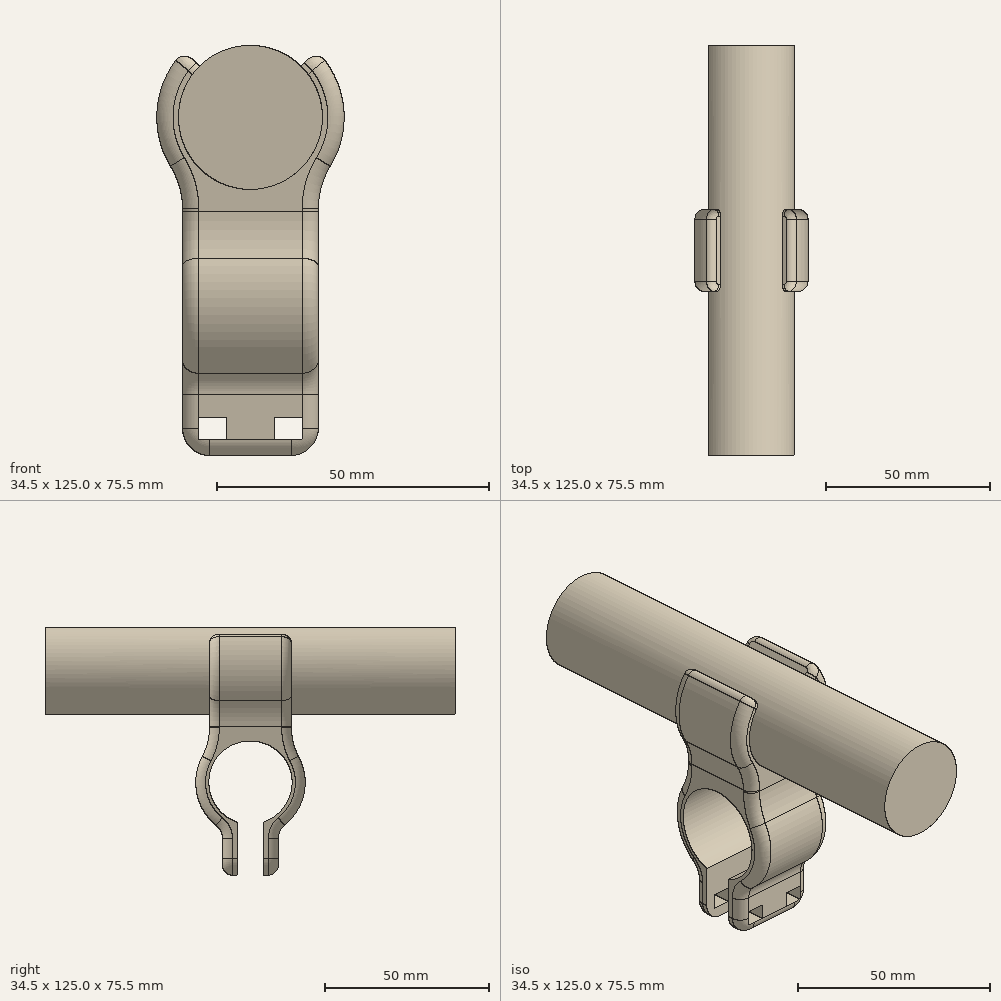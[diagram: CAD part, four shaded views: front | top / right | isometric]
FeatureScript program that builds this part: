
annotation { "Feature Type Name" : "Feature", "Feature Type Description" : "" }
export const myFeature = defineFeature(function(context is Context, id is Id, definition is map)
    precondition{}
    {
        {
            var Q0;
            Q0=qCreatedBy(makeId("Front.planeOp"),FACE);
            var sketch = newSketch(context, id + "F0", { "sketchPlane" : qUnion([Q0])});
            skCircle(sketch, "E0", {"center": v(0, 0) * mm, "radius": 13.25 * mm});
            skSolve(sketch);
        }
        {
            var Q0;
            Q0 = qSketchRegion(id + "F0", true);
            extrude(context, id + "F1", {"entities" : qUnion([Q0]), "endBound" : BoundingType.SYMMETRIC, "depth" : 125 * mm, "offsetDistance" : 25 * mm});
        }
        {
            var Q0;
            Q0=qCreatedBy(makeId("Front.planeOp"),FACE);
            var sketch = newSketch(context, id + "F2", { "sketchPlane" : qUnion([Q0])});
            skArc(sketch, "E1", {"start": v(-12.2, 12.2) * mm, "mid": v(0, -17.25) * mm, "end": v(12.2, 12.2) * mm});
            skArc(sketch, "E2", {"start": v(-9.37, 9.37) * mm, "mid": v(0, -13.25) * mm, "end": v(9.37, 9.37) * mm});
            skLineSegment(sketch, "E3", {"start": v(-9.37, 9.37) * mm, "end": v(-12.2, 12.2) * mm});
            skLineSegment(sketch, "E4", {"start": v(9.37, 9.37) * mm, "end": v(12.2, 12.2) * mm});
            skLineSegment(sketch, "E5", {"start": v(12.2, 12.2) * mm, "end": v(-12.2, 12.2) * mm, "construction": true});
            skSolve(sketch);
        }
        {
            var Q0;
            Q0 = qSketchRegion(id + "F2", true);
            extrude(context, id + "F3", {"entities" : qUnion([Q0]), "endBound" : BoundingType.SYMMETRIC, "depth" : 25 * mm, "offsetDistance" : 25 * mm});
        }
        {
            var Q0;
            Q0=qCreatedBy(makeId("Right.planeOp"),FACE);
            var sketch = newSketch(context, id + "F4", { "sketchPlane" : qUnion([Q0])});
            skArc(sketch, "E6", {"start": v(4, -46.05) * mm, "mid": v(0, -21.3) * mm, "end": v(-4, -46.05) * mm});
            skArc(sketch, "E7", {"start": v(4, -50.21) * mm, "mid": v(0, -17.3) * mm, "end": v(-4, -50.21) * mm});
            skArc(sketch, "E8", {"start": v(-14.8, -26.25) * mm, "mid": v(-13.08, -21.92) * mm, "end": v(-12.5, -17.3) * mm});
            skArc(sketch, "E9", {"start": v(12.5, -17.3) * mm, "mid": v(13.08, -21.92) * mm, "end": v(14.8, -26.25) * mm});
            skLineSegment(sketch, "E10", {"start": v(12.5, -17.3) * mm, "end": v(12.5, -13.25) * mm});
            skLineSegment(sketch, "E11", {"start": v(12.5, -13.25) * mm, "end": v(-12.5, -13.25) * mm});
            skLineSegment(sketch, "E12", {"start": v(-12.5, -13.25) * mm, "end": v(-12.5, -17.3) * mm});
            skPoint(sketch, "E13", {"position": v(0, -17.3) * mm});
            skLineSegment(sketch, "E14.left", {"start": v(-4, -46.05) * mm, "end": v(-4, -50.21) * mm});
            skLineSegment(sketch, "E14.right", {"start": v(4, -46.05) * mm, "end": v(4, -50.21) * mm});
            skLineSegment(sketch, "E15", {"start": v(4, -48.13) * mm, "end": v(-4, -48.13) * mm, "construction": true});
            skLineSegment(sketch, "E16.bottom", {"start": v(-8.5, -48.13) * mm, "end": v(-4, -48.13) * mm});
            skLineSegment(sketch, "E16.top", {"start": v(-8.5, -62.21) * mm, "end": v(-4, -62.21) * mm});
            skLineSegment(sketch, "E16.left", {"start": v(-8.5, -48.13) * mm, "end": v(-8.5, -62.21) * mm});
            skLineSegment(sketch, "E16.right", {"start": v(-4, -48.13) * mm, "end": v(-4, -62.21) * mm});
            skPoint(sketch, "E16.middle", {"position": v(-6.25, -55.17) * mm});
            skLineSegment(sketch, "E17.bottom", {"start": v(4, -48.13) * mm, "end": v(8.5, -48.13) * mm});
            skLineSegment(sketch, "E17.top", {"start": v(4, -62.21) * mm, "end": v(8.5, -62.21) * mm});
            skLineSegment(sketch, "E17.left", {"start": v(4, -48.13) * mm, "end": v(4, -62.21) * mm});
            skLineSegment(sketch, "E17.right", {"start": v(8.5, -48.13) * mm, "end": v(8.5, -62.21) * mm});
            skPoint(sketch, "E17.middle", {"position": v(6.25, -55.17) * mm});
            skSolve(sketch);
        }
        {
            var Q0;
            Q0 = qSketchRegion(id + "F4", true);
            extrude(context, id + "F5", {"entities" : qUnion([Q0]), "operationType" : NewBodyOperationType.ADD, "endBound" : BoundingType.SYMMETRIC, "depth" : 25 * mm, "offsetDistance" : 25 * mm});
        }
        {
            var Q0;
            Q0=makeQuery(id+"F5.opExtrude","SWEPT_FACE",FACE,{"disambiguationData":[OSD([sQuery(id+"F4.wireOp",EDGE,"E16.left")])]});
            var sketch = newSketch(context, id + "F6", { "sketchPlane" : qUnion([Q0])});
            skPoint(sketch, "E18.centerSnap0", {"position": v(12.5, -55.3) * mm});
            skPoint(sketch, "E18.centerSnap1", {"position": v(0, -62.21) * mm});
            skLineSegment(sketch, "E19.bottom", {"start": v(-9.5, -59.21) * mm, "end": v(-4.5, -59.21) * mm});
            skLineSegment(sketch, "E19.top", {"start": v(-9.5, -55.21) * mm, "end": v(-4.5, -55.21) * mm});
            skLineSegment(sketch, "E19.left", {"start": v(-9.5, -59.21) * mm, "end": v(-9.5, -55.21) * mm});
            skLineSegment(sketch, "E19.right", {"start": v(-4.5, -59.21) * mm, "end": v(-4.5, -55.21) * mm});
            skLineSegment(sketch, "E20.bottom", {"start": v(9.5, -59.21) * mm, "end": v(4.5, -59.21) * mm});
            skLineSegment(sketch, "E20.top", {"start": v(9.5, -55.21) * mm, "end": v(4.5, -55.21) * mm});
            skLineSegment(sketch, "E20.left", {"start": v(9.5, -59.21) * mm, "end": v(9.5, -55.21) * mm});
            skLineSegment(sketch, "E20.right", {"start": v(4.5, -59.21) * mm, "end": v(4.5, -55.21) * mm});
            skSolve(sketch);
        }
        {
            var Q0;
            Q0 = qSketchRegion(id + "F6", true);
            extrude(context, id + "F7", {"entities" : qUnion([Q0]), "operationType" : NewBodyOperationType.REMOVE, "endBound" : BoundingType.THROUGH_ALL, "oppositeDirection" : true, "depth" : 25 * mm, "offsetDistance" : 25 * mm});
        }
        {
            var Q0;
            Q0=makeQuery(id+"F5.boolean.opBoolean","INTERSECT",EDGE,{"disambiguationData":[OD(1.0)],"derivedFrom":[makeQuery(id+"F3.opExtrude","SWEPT_FACE",FACE,{"disambiguationData":[OSD([sQuery(id+"F2.wireOp",EDGE,"E1")])]}),makeQuery(id+"F5.opExtrude","SWEPT_FACE",FACE,{"disambiguationData":[OSD([sQuery(id+"F4.wireOp",EDGE,"E11")])]})]});
            var Q1;
            Q1=makeQuery(id+"F5.boolean.opBoolean","INTERSECT",EDGE,{"disambiguationData":[OD(0.0)],"derivedFrom":[makeQuery(id+"F3.opExtrude","SWEPT_FACE",FACE,{"disambiguationData":[OSD([sQuery(id+"F2.wireOp",EDGE,"E1")])]}),makeQuery(id+"F5.opExtrude","SWEPT_FACE",FACE,{"disambiguationData":[OSD([sQuery(id+"F4.wireOp",EDGE,"E11")])]})]});
            fillet(context, id + "F8", {"entities" : qUnion([Q0, Q1]), "tangentPropagation" : true, "radius" : 15 * mm, "defaultsChanged" : true, "vertexSettings" : [], "allowEdgeOverflow" : false});
        }
        {
            var Q0;
            {var subQ0=sQuery(id+"F4.wireOp",EDGE,"E11");Q0=makeQuery(id+"F8.opFillet","BLEND_EDGE",EDGE,{"blendedFrom":[makeQuery(id+"F5.boolean.opBoolean","INTERSECT",EDGE,{"disambiguationData":[OD(0.0)],"derivedFrom":[makeQuery(id+"F3.opExtrude","SWEPT_FACE",FACE,{"disambiguationData":[OSD([sQuery(id+"F2.wireOp",EDGE,"E1")])]}),makeQuery(id+"F5.opExtrude","SWEPT_FACE",FACE,{"disambiguationData":[OSD([subQ0])]})]}),makeQuery(id+"F5.opExtrude","CAP_FACE",FACE,{"disambiguationData":[OSD([sQuery(id+"F4.wireOp",EDGE,"E6"),sQuery(id+"F4.wireOp",EDGE,"E7"),sQuery(id+"F4.wireOp",EDGE,"E8"),sQuery(id+"F4.wireOp",EDGE,"E9"),sQuery(id+"F4.wireOp",EDGE,"E10"),subQ0,sQuery(id+"F4.wireOp",EDGE,"E12"),sQuery(id+"F4.wireOp",EDGE,"E14.left"),sQuery(id+"F4.wireOp",EDGE,"E14.right"),sQuery(id+"F4.wireOp",EDGE,"E16.top"),sQuery(id+"F4.wireOp",EDGE,"E16.left"),sQuery(id+"F4.wireOp",EDGE,"E16.right"),sQuery(id+"F4.wireOp",EDGE,"E17.top"),sQuery(id+"F4.wireOp",EDGE,"E17.left"),sQuery(id+"F4.wireOp",EDGE,"E17.right")])],"isStart":true})],"blendedInto":[makeQuery(id+"F5.opExtrude","CAP_FACE",FACE,{"disambiguationData":[OSD([sQuery(id+"F4.wireOp",EDGE,"E6"),sQuery(id+"F4.wireOp",EDGE,"E7"),sQuery(id+"F4.wireOp",EDGE,"E8"),sQuery(id+"F4.wireOp",EDGE,"E9"),sQuery(id+"F4.wireOp",EDGE,"E10"),subQ0,sQuery(id+"F4.wireOp",EDGE,"E12"),sQuery(id+"F4.wireOp",EDGE,"E14.left"),sQuery(id+"F4.wireOp",EDGE,"E14.right"),sQuery(id+"F4.wireOp",EDGE,"E16.top"),sQuery(id+"F4.wireOp",EDGE,"E16.left"),sQuery(id+"F4.wireOp",EDGE,"E16.right"),sQuery(id+"F4.wireOp",EDGE,"E17.top"),sQuery(id+"F4.wireOp",EDGE,"E17.left"),sQuery(id+"F4.wireOp",EDGE,"E17.right")])],"isStart":true})]});}
            var Q1;
            {var subQ0=sQuery(id+"F4.wireOp",EDGE,"E11");Q1=makeQuery(id+"F8.opFillet","BLEND_EDGE",EDGE,{"blendedFrom":[makeQuery(id+"F5.boolean.opBoolean","INTERSECT",EDGE,{"disambiguationData":[OD(1.0)],"derivedFrom":[makeQuery(id+"F3.opExtrude","SWEPT_FACE",FACE,{"disambiguationData":[OSD([sQuery(id+"F2.wireOp",EDGE,"E1")])]}),makeQuery(id+"F5.opExtrude","SWEPT_FACE",FACE,{"disambiguationData":[OSD([subQ0])]})]}),makeQuery(id+"F5.opExtrude","CAP_FACE",FACE,{"disambiguationData":[OSD([sQuery(id+"F4.wireOp",EDGE,"E6"),sQuery(id+"F4.wireOp",EDGE,"E7"),sQuery(id+"F4.wireOp",EDGE,"E8"),sQuery(id+"F4.wireOp",EDGE,"E9"),sQuery(id+"F4.wireOp",EDGE,"E10"),subQ0,sQuery(id+"F4.wireOp",EDGE,"E12"),sQuery(id+"F4.wireOp",EDGE,"E14.left"),sQuery(id+"F4.wireOp",EDGE,"E14.right"),sQuery(id+"F4.wireOp",EDGE,"E16.top"),sQuery(id+"F4.wireOp",EDGE,"E16.left"),sQuery(id+"F4.wireOp",EDGE,"E16.right"),sQuery(id+"F4.wireOp",EDGE,"E17.top"),sQuery(id+"F4.wireOp",EDGE,"E17.left"),sQuery(id+"F4.wireOp",EDGE,"E17.right")])],"isStart":false})],"blendedInto":[makeQuery(id+"F5.opExtrude","CAP_FACE",FACE,{"disambiguationData":[OSD([sQuery(id+"F4.wireOp",EDGE,"E6"),sQuery(id+"F4.wireOp",EDGE,"E7"),sQuery(id+"F4.wireOp",EDGE,"E8"),sQuery(id+"F4.wireOp",EDGE,"E9"),sQuery(id+"F4.wireOp",EDGE,"E10"),subQ0,sQuery(id+"F4.wireOp",EDGE,"E12"),sQuery(id+"F4.wireOp",EDGE,"E14.left"),sQuery(id+"F4.wireOp",EDGE,"E14.right"),sQuery(id+"F4.wireOp",EDGE,"E16.top"),sQuery(id+"F4.wireOp",EDGE,"E16.left"),sQuery(id+"F4.wireOp",EDGE,"E16.right"),sQuery(id+"F4.wireOp",EDGE,"E17.top"),sQuery(id+"F4.wireOp",EDGE,"E17.left"),sQuery(id+"F4.wireOp",EDGE,"E17.right")])],"isStart":false})]});}
            fillet(context, id + "F9", {"entities" : qUnion([Q0, Q1]), "tangentPropagation" : true, "radius" : 15 * mm, "defaultsChanged" : false, "vertexSettings" : [], "allowEdgeOverflow" : false});
        }
        {
            var Q0;
            Q0=makeQuery(id+"F5.opExtrude","CAP_EDGE",EDGE,{"disambiguationData":[OSD([sQuery(id+"F4.wireOp",EDGE,"E16.top")])],"isStart":false});
            var Q1;
            Q1=makeQuery(id+"F5.opExtrude","CAP_EDGE",EDGE,{"disambiguationData":[OSD([sQuery(id+"F4.wireOp",EDGE,"E17.top")])],"isStart":false});
            var Q2;
            Q2=makeQuery(id+"F5.opExtrude","CAP_EDGE",EDGE,{"disambiguationData":[OSD([sQuery(id+"F4.wireOp",EDGE,"E16.top")])],"isStart":true});
            var Q3;
            Q3=makeQuery(id+"F5.opExtrude","CAP_EDGE",EDGE,{"disambiguationData":[OSD([sQuery(id+"F4.wireOp",EDGE,"E17.top")])],"isStart":true});
            var Q4;
            Q4=makeQuery(id+"F5.opExtrude","SWEPT_EDGE",EDGE,{"disambiguationData":[OSD([sQuery(id+"F4.wireOp",EDGE,"E7"),sQuery(id+"F4.wireOp",EDGE,"E16.left")])]});
            var Q5;
            Q5=makeQuery(id+"F5.opExtrude","SWEPT_EDGE",EDGE,{"disambiguationData":[OSD([sQuery(id+"F4.wireOp",EDGE,"E7"),sQuery(id+"F4.wireOp",EDGE,"E17.right")])]});
            fillet(context, id + "F10", {"entities" : qUnion([Q0, Q1, Q2, Q3, Q4, Q5]), "tangentPropagation" : true, "radius" : 5 * mm, "defaultsChanged" : false, "vertexSettings" : [], "allowEdgeOverflow" : false});
        }
        {
            var Q0;
            {var subQ0=sQuery(id+"F4.wireOp",EDGE,"E17.right");var subQ1=sQuery(id+"F4.wireOp",EDGE,"E7");Q0=makeQuery(id+"F10.opFillet","BLEND_EDGE",EDGE,{"blendedFrom":[makeQuery(id+"F5.opExtrude","SWEPT_EDGE",EDGE,{"disambiguationData":[OSD([subQ1,subQ0])]}),makeQuery(id+"F5.opExtrude","CAP_FACE",FACE,{"disambiguationData":[OSD([sQuery(id+"F4.wireOp",EDGE,"E6"),subQ1,sQuery(id+"F4.wireOp",EDGE,"E8"),sQuery(id+"F4.wireOp",EDGE,"E9"),sQuery(id+"F4.wireOp",EDGE,"E10"),sQuery(id+"F4.wireOp",EDGE,"E11"),sQuery(id+"F4.wireOp",EDGE,"E12"),sQuery(id+"F4.wireOp",EDGE,"E14.left"),sQuery(id+"F4.wireOp",EDGE,"E14.right"),sQuery(id+"F4.wireOp",EDGE,"E16.top"),sQuery(id+"F4.wireOp",EDGE,"E16.left"),sQuery(id+"F4.wireOp",EDGE,"E16.right"),sQuery(id+"F4.wireOp",EDGE,"E17.top"),sQuery(id+"F4.wireOp",EDGE,"E17.left"),subQ0])],"isStart":false})],"blendedInto":[makeQuery(id+"F5.opExtrude","CAP_FACE",FACE,{"disambiguationData":[OSD([sQuery(id+"F4.wireOp",EDGE,"E6"),subQ1,sQuery(id+"F4.wireOp",EDGE,"E8"),sQuery(id+"F4.wireOp",EDGE,"E9"),sQuery(id+"F4.wireOp",EDGE,"E10"),sQuery(id+"F4.wireOp",EDGE,"E11"),sQuery(id+"F4.wireOp",EDGE,"E12"),sQuery(id+"F4.wireOp",EDGE,"E14.left"),sQuery(id+"F4.wireOp",EDGE,"E14.right"),sQuery(id+"F4.wireOp",EDGE,"E16.top"),sQuery(id+"F4.wireOp",EDGE,"E16.left"),sQuery(id+"F4.wireOp",EDGE,"E16.right"),sQuery(id+"F4.wireOp",EDGE,"E17.top"),sQuery(id+"F4.wireOp",EDGE,"E17.left"),subQ0])],"isStart":false})]});}
            var Q1;
            {var subQ0=sQuery(id+"F4.wireOp",EDGE,"E16.left");var subQ1=sQuery(id+"F4.wireOp",EDGE,"E7");Q1=makeQuery(id+"F10.opFillet","BLEND_EDGE",EDGE,{"blendedFrom":[makeQuery(id+"F5.opExtrude","SWEPT_EDGE",EDGE,{"disambiguationData":[OSD([subQ1,subQ0])]}),makeQuery(id+"F5.opExtrude","CAP_FACE",FACE,{"disambiguationData":[OSD([sQuery(id+"F4.wireOp",EDGE,"E6"),subQ1,sQuery(id+"F4.wireOp",EDGE,"E8"),sQuery(id+"F4.wireOp",EDGE,"E9"),sQuery(id+"F4.wireOp",EDGE,"E10"),sQuery(id+"F4.wireOp",EDGE,"E11"),sQuery(id+"F4.wireOp",EDGE,"E12"),sQuery(id+"F4.wireOp",EDGE,"E14.left"),sQuery(id+"F4.wireOp",EDGE,"E14.right"),sQuery(id+"F4.wireOp",EDGE,"E16.top"),subQ0,sQuery(id+"F4.wireOp",EDGE,"E16.right"),sQuery(id+"F4.wireOp",EDGE,"E17.top"),sQuery(id+"F4.wireOp",EDGE,"E17.left"),sQuery(id+"F4.wireOp",EDGE,"E17.right")])],"isStart":false})],"blendedInto":[makeQuery(id+"F5.opExtrude","CAP_FACE",FACE,{"disambiguationData":[OSD([sQuery(id+"F4.wireOp",EDGE,"E6"),subQ1,sQuery(id+"F4.wireOp",EDGE,"E8"),sQuery(id+"F4.wireOp",EDGE,"E9"),sQuery(id+"F4.wireOp",EDGE,"E10"),sQuery(id+"F4.wireOp",EDGE,"E11"),sQuery(id+"F4.wireOp",EDGE,"E12"),sQuery(id+"F4.wireOp",EDGE,"E14.left"),sQuery(id+"F4.wireOp",EDGE,"E14.right"),sQuery(id+"F4.wireOp",EDGE,"E16.top"),subQ0,sQuery(id+"F4.wireOp",EDGE,"E16.right"),sQuery(id+"F4.wireOp",EDGE,"E17.top"),sQuery(id+"F4.wireOp",EDGE,"E17.left"),sQuery(id+"F4.wireOp",EDGE,"E17.right")])],"isStart":false})]});}
            var Q2;
            Q2=makeQuery(id+"F5.opExtrude","CAP_EDGE",EDGE,{"disambiguationData":[OSD([sQuery(id+"F4.wireOp",EDGE,"E9")])],"isStart":false});
            var Q3;
            {var subQ0=sQuery(id+"F4.wireOp",EDGE,"E9");var subQ1=sQuery(id+"F4.wireOp",EDGE,"E7");var subQ2=makeQuery(id+"F4.imprint","INTERSECT",VERTEX,{"disambiguationData":[OD(0.0)],"derivedFrom":[subQ1,subQ0]});Q3=makeQuery(id+"F5.opExtrude","CAP_EDGE",EDGE,{"disambiguationData":[OSD([subQ1]),TDD([makeQuery(id+"F4.imprint","IMPRINT",EDGE,{"disambiguationData":[TD([[subQ2,1.0]])],"derivedFrom":subQ1}),makeQuery(id+"F4.imprint","IMPRINT",EDGE,{"disambiguationData":[TD([[subQ2,-1.0]])],"derivedFrom":subQ1})])],"isStart":false});}
            var Q4;
            Q4=makeQuery(id+"F5.opExtrude","CAP_EDGE",EDGE,{"disambiguationData":[OSD([sQuery(id+"F4.wireOp",EDGE,"E8")])],"isStart":false});
            var Q5;
            {var subQ0=sQuery(id+"F4.wireOp",EDGE,"E8");var subQ1=sQuery(id+"F4.wireOp",EDGE,"E7");var subQ2=makeQuery(id+"F4.imprint","INTERSECT",VERTEX,{"disambiguationData":[OD(0.0)],"derivedFrom":[subQ1,subQ0]});Q5=makeQuery(id+"F5.opExtrude","CAP_EDGE",EDGE,{"disambiguationData":[OSD([subQ1]),TDD([makeQuery(id+"F4.imprint","IMPRINT",EDGE,{"disambiguationData":[TD([[subQ2,1.0]])],"derivedFrom":subQ1}),makeQuery(id+"F4.imprint","IMPRINT",EDGE,{"disambiguationData":[TD([[subQ2,-1.0]])],"derivedFrom":subQ1})])],"isStart":false});}
            var Q6;
            Q6=makeQuery(id+"F5.opExtrude","CAP_EDGE",EDGE,{"disambiguationData":[OSD([sQuery(id+"F4.wireOp",EDGE,"E16.left")])],"isStart":false});
            var Q7;
            Q7=makeQuery(id+"F5.opExtrude","CAP_EDGE",EDGE,{"disambiguationData":[OSD([sQuery(id+"F4.wireOp",EDGE,"E17.right")])],"isStart":false});
            var Q8;
            Q8=makeQuery(id+"F10.opFillet","BLEND_EDGE",EDGE,{"blendedFrom":[makeQuery(id+"F5.opExtrude","CAP_EDGE",EDGE,{"disambiguationData":[OSD([sQuery(id+"F4.wireOp",EDGE,"E17.top")])],"isStart":false}),makeQuery(id+"F5.opExtrude","SWEPT_FACE",FACE,{"disambiguationData":[OSD([sQuery(id+"F4.wireOp",EDGE,"E17.right")])]})],"blendedInto":[makeQuery(id+"F5.opExtrude","SWEPT_FACE",FACE,{"disambiguationData":[OSD([sQuery(id+"F4.wireOp",EDGE,"E17.right")])]})]});
            var Q9;
            Q9=makeQuery(id+"F10.opFillet","BLEND_EDGE",EDGE,{"blendedFrom":[makeQuery(id+"F5.opExtrude","CAP_EDGE",EDGE,{"disambiguationData":[OSD([sQuery(id+"F4.wireOp",EDGE,"E16.top")])],"isStart":false}),makeQuery(id+"F5.opExtrude","SWEPT_FACE",FACE,{"disambiguationData":[OSD([sQuery(id+"F4.wireOp",EDGE,"E16.left")])]})],"blendedInto":[makeQuery(id+"F5.opExtrude","SWEPT_FACE",FACE,{"disambiguationData":[OSD([sQuery(id+"F4.wireOp",EDGE,"E16.left")])]})]});
            var Q10;
            Q10=makeQuery(id+"F5.opExtrude","SWEPT_EDGE",EDGE,{"disambiguationData":[OSD([sQuery(id+"F4.wireOp",EDGE,"E17.top"),sQuery(id+"F4.wireOp",EDGE,"E17.right")])]});
            var Q11;
            {var subQ0=sQuery(id+"F4.wireOp",EDGE,"E10");var subQ1=sQuery(id+"F2.wireOp",EDGE,"E1");var subQ2=sQuery(id+"F4.wireOp",EDGE,"E11");Q11=makeQuery(id+"F9.opFillet","BLEND_EDGE",EDGE,{"blendedFrom":[makeQuery(id+"F8.opFillet","BLEND_EDGE",EDGE,{"blendedFrom":[makeQuery(id+"F5.boolean.opBoolean","INTERSECT",EDGE,{"disambiguationData":[OD(1.0)],"derivedFrom":[makeQuery(id+"F3.opExtrude","SWEPT_FACE",FACE,{"disambiguationData":[OSD([subQ1])]}),makeQuery(id+"F5.opExtrude","SWEPT_FACE",FACE,{"disambiguationData":[OSD([subQ2])]})]}),makeQuery(id+"F5.opExtrude","CAP_FACE",FACE,{"disambiguationData":[OSD([sQuery(id+"F4.wireOp",EDGE,"E6"),sQuery(id+"F4.wireOp",EDGE,"E7"),sQuery(id+"F4.wireOp",EDGE,"E8"),sQuery(id+"F4.wireOp",EDGE,"E9"),subQ0,subQ2,sQuery(id+"F4.wireOp",EDGE,"E12"),sQuery(id+"F4.wireOp",EDGE,"E14.left"),sQuery(id+"F4.wireOp",EDGE,"E14.right"),sQuery(id+"F4.wireOp",EDGE,"E16.top"),sQuery(id+"F4.wireOp",EDGE,"E16.left"),sQuery(id+"F4.wireOp",EDGE,"E16.right"),sQuery(id+"F4.wireOp",EDGE,"E17.top"),sQuery(id+"F4.wireOp",EDGE,"E17.left"),sQuery(id+"F4.wireOp",EDGE,"E17.right")])],"isStart":false})],"blendedInto":[makeQuery(id+"F5.opExtrude","CAP_FACE",FACE,{"disambiguationData":[OSD([sQuery(id+"F4.wireOp",EDGE,"E6"),sQuery(id+"F4.wireOp",EDGE,"E7"),sQuery(id+"F4.wireOp",EDGE,"E8"),sQuery(id+"F4.wireOp",EDGE,"E9"),subQ0,subQ2,sQuery(id+"F4.wireOp",EDGE,"E12"),sQuery(id+"F4.wireOp",EDGE,"E14.left"),sQuery(id+"F4.wireOp",EDGE,"E14.right"),sQuery(id+"F4.wireOp",EDGE,"E16.top"),sQuery(id+"F4.wireOp",EDGE,"E16.left"),sQuery(id+"F4.wireOp",EDGE,"E16.right"),sQuery(id+"F4.wireOp",EDGE,"E17.top"),sQuery(id+"F4.wireOp",EDGE,"E17.left"),sQuery(id+"F4.wireOp",EDGE,"E17.right")])],"isStart":false})]}),makeQuery(id+"F5.boolean.opBoolean","MERGE",FACE,{"derivedFrom":[makeQuery(id+"F3.opExtrude","CAP_FACE",FACE,{"disambiguationData":[OSD([subQ1,sQuery(id+"F2.wireOp",EDGE,"E2"),sQuery(id+"F2.wireOp",EDGE,"E3"),sQuery(id+"F2.wireOp",EDGE,"E4")])],"isStart":true}),makeQuery(id+"F5.opExtrude","SWEPT_FACE",FACE,{"disambiguationData":[OSD([subQ0])]})]})],"blendedInto":[makeQuery(id+"F5.boolean.opBoolean","MERGE",FACE,{"derivedFrom":[makeQuery(id+"F3.opExtrude","CAP_FACE",FACE,{"disambiguationData":[OSD([subQ1,sQuery(id+"F2.wireOp",EDGE,"E2"),sQuery(id+"F2.wireOp",EDGE,"E3"),sQuery(id+"F2.wireOp",EDGE,"E4")])],"isStart":true}),makeQuery(id+"F5.opExtrude","SWEPT_FACE",FACE,{"disambiguationData":[OSD([subQ0])]})]})]});}
            var Q12;
            {var subQ0=sQuery(id+"F4.wireOp",EDGE,"E12");var subQ1=sQuery(id+"F2.wireOp",EDGE,"E1");var subQ2=sQuery(id+"F4.wireOp",EDGE,"E11");Q12=makeQuery(id+"F9.opFillet","BLEND_EDGE",EDGE,{"blendedFrom":[makeQuery(id+"F8.opFillet","BLEND_EDGE",EDGE,{"blendedFrom":[makeQuery(id+"F5.boolean.opBoolean","INTERSECT",EDGE,{"disambiguationData":[OD(1.0)],"derivedFrom":[makeQuery(id+"F3.opExtrude","SWEPT_FACE",FACE,{"disambiguationData":[OSD([subQ1])]}),makeQuery(id+"F5.opExtrude","SWEPT_FACE",FACE,{"disambiguationData":[OSD([subQ2])]})]}),makeQuery(id+"F5.opExtrude","CAP_FACE",FACE,{"disambiguationData":[OSD([sQuery(id+"F4.wireOp",EDGE,"E6"),sQuery(id+"F4.wireOp",EDGE,"E7"),sQuery(id+"F4.wireOp",EDGE,"E8"),sQuery(id+"F4.wireOp",EDGE,"E9"),sQuery(id+"F4.wireOp",EDGE,"E10"),subQ2,subQ0,sQuery(id+"F4.wireOp",EDGE,"E14.left"),sQuery(id+"F4.wireOp",EDGE,"E14.right"),sQuery(id+"F4.wireOp",EDGE,"E16.top"),sQuery(id+"F4.wireOp",EDGE,"E16.left"),sQuery(id+"F4.wireOp",EDGE,"E16.right"),sQuery(id+"F4.wireOp",EDGE,"E17.top"),sQuery(id+"F4.wireOp",EDGE,"E17.left"),sQuery(id+"F4.wireOp",EDGE,"E17.right")])],"isStart":false})],"blendedInto":[makeQuery(id+"F5.opExtrude","CAP_FACE",FACE,{"disambiguationData":[OSD([sQuery(id+"F4.wireOp",EDGE,"E6"),sQuery(id+"F4.wireOp",EDGE,"E7"),sQuery(id+"F4.wireOp",EDGE,"E8"),sQuery(id+"F4.wireOp",EDGE,"E9"),sQuery(id+"F4.wireOp",EDGE,"E10"),subQ2,subQ0,sQuery(id+"F4.wireOp",EDGE,"E14.left"),sQuery(id+"F4.wireOp",EDGE,"E14.right"),sQuery(id+"F4.wireOp",EDGE,"E16.top"),sQuery(id+"F4.wireOp",EDGE,"E16.left"),sQuery(id+"F4.wireOp",EDGE,"E16.right"),sQuery(id+"F4.wireOp",EDGE,"E17.top"),sQuery(id+"F4.wireOp",EDGE,"E17.left"),sQuery(id+"F4.wireOp",EDGE,"E17.right")])],"isStart":false})]}),makeQuery(id+"F5.boolean.opBoolean","MERGE",FACE,{"derivedFrom":[makeQuery(id+"F3.opExtrude","CAP_FACE",FACE,{"disambiguationData":[OSD([subQ1,sQuery(id+"F2.wireOp",EDGE,"E2"),sQuery(id+"F2.wireOp",EDGE,"E3"),sQuery(id+"F2.wireOp",EDGE,"E4")])],"isStart":false}),makeQuery(id+"F5.opExtrude","SWEPT_FACE",FACE,{"disambiguationData":[OSD([subQ0])]})]})],"blendedInto":[makeQuery(id+"F5.boolean.opBoolean","MERGE",FACE,{"derivedFrom":[makeQuery(id+"F3.opExtrude","CAP_FACE",FACE,{"disambiguationData":[OSD([subQ1,sQuery(id+"F2.wireOp",EDGE,"E2"),sQuery(id+"F2.wireOp",EDGE,"E3"),sQuery(id+"F2.wireOp",EDGE,"E4")])],"isStart":false}),makeQuery(id+"F5.opExtrude","SWEPT_FACE",FACE,{"disambiguationData":[OSD([subQ0])]})]})]});}
            var Q13;
            Q13=makeQuery(id+"F5.opExtrude","CAP_EDGE",EDGE,{"disambiguationData":[OSD([sQuery(id+"F4.wireOp",EDGE,"E9")])],"isStart":true});
            var Q14;
            Q14=makeQuery(id+"F5.opExtrude","CAP_EDGE",EDGE,{"disambiguationData":[OSD([sQuery(id+"F4.wireOp",EDGE,"E8")])],"isStart":true});
            fillet(context, id + "F11", {"entities" : qUnion([Q0, Q1, Q2, Q3, Q4, Q5, Q6, Q7, Q8, Q9, Q10, Q11, Q12, Q13, Q14]), "tangentPropagation" : true, "radius" : 3 * mm, "defaultsChanged" : false, "vertexSettings" : [], "allowEdgeOverflow" : false});
        }
        {
            var Q0;
            Q0=makeQuery(id+"F3.opExtrude","SWEPT_EDGE",EDGE,{"disambiguationData":[OSD([sQuery(id+"F2.wireOp",EDGE,"E1"),sQuery(id+"F2.wireOp",EDGE,"E4")])]});
            var Q1;
            Q1=makeQuery(id+"F3.opExtrude","SWEPT_EDGE",EDGE,{"disambiguationData":[OSD([sQuery(id+"F2.wireOp",EDGE,"E1"),sQuery(id+"F2.wireOp",EDGE,"E3")])]});
            fillet(context, id + "F12", {"entities" : qUnion([Q0, Q1]), "tangentPropagation" : true, "radius" : 2 * mm, "defaultsChanged" : true, "vertexSettings" : [], "allowEdgeOverflow" : false});
        }
    });
